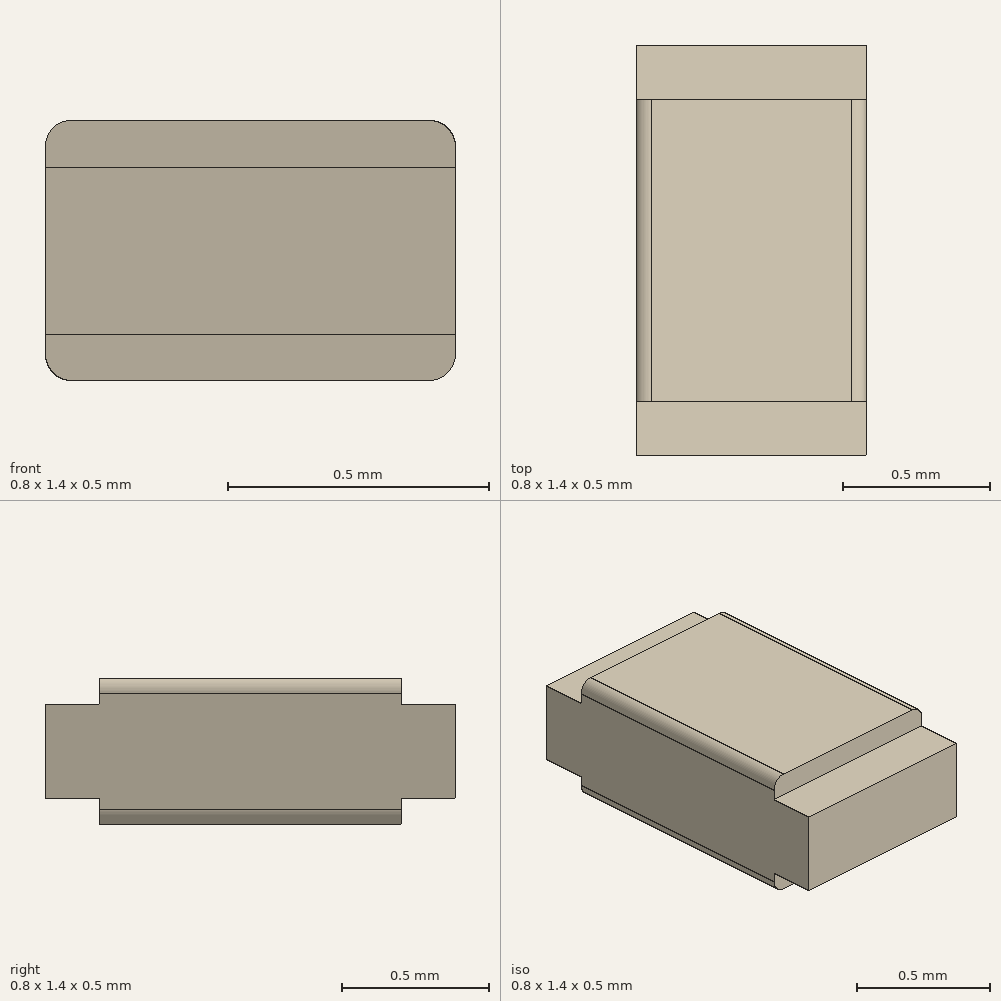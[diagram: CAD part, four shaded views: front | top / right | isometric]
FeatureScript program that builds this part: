
annotation { "Feature Type Name" : "Feature", "Feature Type Description" : "" }
export const myFeature = defineFeature(function(context is Context, id is Id, definition is map)
    precondition{}
    {
        {
            var Q0;
            Q0=qCreatedBy(makeId("Right.planeOp"),FACE);
            var sketch = newSketch(context, id + "F0", { "sketchPlane" : qUnion([Q0])});
            skLineSegment(sketch, "E0.rect.bottom", {"start": v(0.8, 0.25) * mm, "end": v(-0.8, 0.25) * mm});
            skLineSegment(sketch, "E0.rect.top", {"start": v(0.8, -0.25) * mm, "end": v(-0.8, -0.25) * mm});
            skLineSegment(sketch, "E0.rect.left", {"start": v(0.8, 0.25) * mm, "end": v(0.8, -0.25) * mm});
            skLineSegment(sketch, "E0.rect.right", {"start": v(-0.8, 0.25) * mm, "end": v(-0.8, -0.25) * mm});
            skPoint(sketch, "E0.rect.middle", {"position": v(0, 0) * mm});
            skLineSegment(sketch, "E1", {"start": v(-0.51, 0.25) * mm, "end": v(-0.51, 0.16) * mm});
            skLineSegment(sketch, "E2", {"start": v(-0.51, 0.16) * mm, "end": v(-0.7, 0.16) * mm});
            skLineSegment(sketch, "E3", {"start": v(-0.7, 0.16) * mm, "end": v(-0.7, -0.16) * mm});
            skLineSegment(sketch, "E4", {"start": v(-0.7, -0.16) * mm, "end": v(-0.51, -0.16) * mm});
            skLineSegment(sketch, "E5", {"start": v(-0.51, -0.16) * mm, "end": v(-0.51, -0.25) * mm});
            skLineSegment(sketch, "E6.MirrorCS", {"start": v(0.51, 0.25) * mm, "end": v(0.51, 0.16) * mm});
            skLineSegment(sketch, "E7.MirrorCS", {"start": v(0.51, 0.16) * mm, "end": v(0.7, 0.16) * mm});
            skLineSegment(sketch, "E8.MirrorCS", {"start": v(0.7, 0.16) * mm, "end": v(0.7, -0.16) * mm});
            skLineSegment(sketch, "E9.MirrorCS", {"start": v(0.7, -0.16) * mm, "end": v(0.51, -0.16) * mm});
            skLineSegment(sketch, "E10.MirrorCS", {"start": v(0.51, -0.16) * mm, "end": v(0.51, -0.25) * mm});
            skLineSegment(sketch, "E11.left", {"start": v(0.51, 0.24) * mm, "end": v(0.51, -0.24) * mm});
            skLineSegment(sketch, "E11.right", {"start": v(-0.51, 0.24) * mm, "end": v(-0.51, -0.24) * mm});
            skSolve(sketch);
        }
        {
            var Q0;
            {var subQ4=sQuery(id+"F0.wireOp",EDGE,"E11.bottom");Q0=makeQuery(id+"F0.imprint","IMPRINT",FACE,{"disambiguationData":[TD([[makeQuery(id+"F0.imprint","IMPRINT",EDGE,{"derivedFrom":subQ4}),1.0]])]});}
            var Q1;
            {var subQ2=sQuery(id+"F0.wireOp",EDGE,"E2");Q1=makeQuery(id+"F0.imprint","IMPRINT",FACE,{"disambiguationData":[TD([[makeQuery(id+"F0.imprint","IMPRINT",EDGE,{"derivedFrom":subQ2}),1.0]])]});}
            var Q2;
            {var subQ2=sQuery(id+"F0.wireOp",EDGE,"E7.MirrorCS");Q2=makeQuery(id+"F0.imprint","IMPRINT",FACE,{"disambiguationData":[TD([[makeQuery(id+"F0.imprint","IMPRINT",EDGE,{"derivedFrom":subQ2}),-1.0]])]});}
            var Q3;
            {var subQ4=sQuery(id+"F0.wireOp",EDGE,"E1");Q3=makeQuery(id+"F0.imprint","IMPRINT",FACE,{"disambiguationData":[TD([[makeQuery(id+"F0.imprint","IMPRINT",EDGE,{"derivedFrom":subQ4}),1.0]])]});}
            extrude(context, id + "F1", {"entities" : qUnion([Q0, Q1, Q2, Q3]), "endBound" : BoundingType.SYMMETRIC, "depth" : 0.79 * mm});
        }
        {
            var Q0;
            Q0=makeQuery(id+"F1.opExtrude","CAP_EDGE",EDGE,{"disambiguationData":[OSD([sQuery(id+"F0.wireOp",EDGE,"E0.rect.bottom")])],"isStart":true});
            var Q1;
            Q1=makeQuery(id+"F1.opExtrude","CAP_EDGE",EDGE,{"disambiguationData":[OSD([sQuery(id+"F0.wireOp",EDGE,"E0.rect.bottom")])],"isStart":false});
            var Q2;
            Q2=makeQuery(id+"F1.opExtrude","CAP_EDGE",EDGE,{"disambiguationData":[OSD([sQuery(id+"F0.wireOp",EDGE,"E0.rect.top")])],"isStart":false});
            var Q3;
            Q3=makeQuery(id+"F1.opExtrude","CAP_EDGE",EDGE,{"disambiguationData":[OSD([sQuery(id+"F0.wireOp",EDGE,"E0.rect.top")])],"isStart":true});
            fillet(context, id + "F2", {"entities" : qUnion([Q0, Q1, Q2, Q3]), "radius" : 0.05 * mm, "allowEdgeOverflow" : false});
        }
    });
